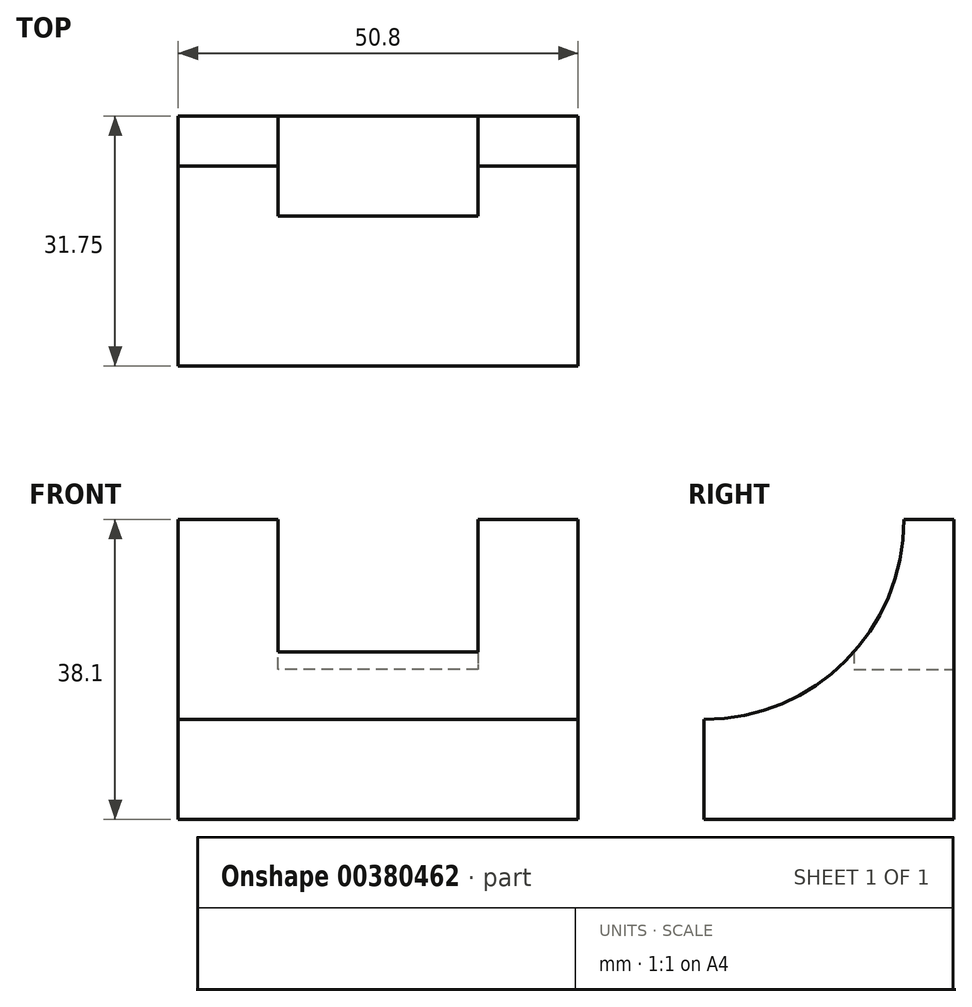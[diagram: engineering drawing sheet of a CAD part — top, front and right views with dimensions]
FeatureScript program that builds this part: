
annotation { "Feature Type Name" : "Feature", "Feature Type Description" : "" }
export const myFeature = defineFeature(function(context is Context, id is Id, definition is map)
    precondition{}
    {
        {
            var Q0;
            Q0=qCreatedBy(makeId("Front.planeOp"),FACE);
            var sketch = newSketch(context, id + "F0", { "sketchPlane" : qUnion([Q0])});
            skLineSegment(sketch, "E0", {"start": v(0, 38.1) * mm, "end": v(0, 0) * mm});
            skLineSegment(sketch, "E1", {"start": v(0, 0) * mm, "end": v(50.8, 0) * mm});
            skLineSegment(sketch, "E2", {"start": v(0, 38.1) * mm, "end": v(50.8, 38.1) * mm});
            skLineSegment(sketch, "E3", {"start": v(50.8, 38.1) * mm, "end": v(50.8, 0) * mm});
            skSolve(sketch);
        }
        {
            var Q0;
            Q0 = qSketchRegion(id + "F0", true);
            extrude(context, id + "F1", {"entities" : qUnion([Q0]), "depth" : 31.75 * mm});
        }
        {
            var Q0;
            Q0=makeQuery(id+"F1.opExtrude","CAP_FACE",FACE,{"disambiguationData":[OSD([sQuery(id+"F0.wireOp",EDGE,"E0"),sQuery(id+"F0.wireOp",EDGE,"E1"),sQuery(id+"F0.wireOp",EDGE,"E2"),sQuery(id+"F0.wireOp",EDGE,"E3")])],"isStart":true});
            var sketch = newSketch(context, id + "F2", { "sketchPlane" : qUnion([Q0])});
            skLineSegment(sketch, "E4", {"start": v(-38.1, 38.1) * mm, "end": v(-38.1, 19.05) * mm});
            skLineSegment(sketch, "E5", {"start": v(-38.1, 19.05) * mm, "end": v(-12.7, 19.05) * mm});
            skLineSegment(sketch, "E6", {"start": v(-12.7, 19.05) * mm, "end": v(-12.7, 38.1) * mm});
            skSolve(sketch);
        }
        {
            var Q0;
            Q0 = qSketchRegion(id + "F2", true);
            var Q1;
            {var subQ0=sQuery(id+"F2.wireOp",EDGE,"E4");Q1=makeQuery(id+"F2.imprint","IMPRINT",FACE,{"disambiguationData":[TD([[makeQuery(id+"F2.imprint","IMPRINT",EDGE,{"derivedFrom":subQ0}),1.0]])]});}
            extrude(context, id + "F3", {"entities" : qUnion([Q0, Q1]), "operationType" : NewBodyOperationType.REMOVE, "oppositeDirection" : true, "depth" : 12.7 * mm});
        }
        {
            var Q0;
            Q0=makeQuery(id+"F1.opExtrude","SWEPT_FACE",FACE,{"disambiguationData":[OSD([sQuery(id+"F0.wireOp",EDGE,"E3")])]});
            var sketch = newSketch(context, id + "F4", { "sketchPlane" : qUnion([Q0])});
            skCircle(sketch, "E7", {"center": v(-31.75, 38.1) * mm, "radius": 25.4 * mm});
            skSolve(sketch);
        }
        {
            var Q0;
            {var subQ0=sQuery(id+"F4.wireOp",EDGE,"E7");var subQ1=sQuery(id+"F0.wireOp",EDGE,"E3");var subQ4=makeQuery(id+"F1.opExtrude","CAP_EDGE",EDGE,{"disambiguationData":[OSD([subQ1])],"isStart":false});var subQ5=makeQuery(id+"F4.imprint","INTERSECT",VERTEX,{"derivedFrom":[subQ4,subQ0]});Q0=makeQuery(id+"F4.imprint","IMPRINT",FACE,{"disambiguationData":[TD([[makeQuery(id+"F4.imprint","IMPRINT",EDGE,{"disambiguationData":[TD([[subQ5,-1.0]])],"derivedFrom":subQ0}),1.0]])]});}
            var Q1;
            {var subQ0=sQuery(id+"F4.wireOp",EDGE,"E7");var subQ1=sQuery(id+"F0.wireOp",EDGE,"E3");var subQ4=makeQuery(id+"F1.opExtrude","CAP_EDGE",EDGE,{"disambiguationData":[OSD([subQ1])],"isStart":false});var subQ5=makeQuery(id+"F4.imprint","INTERSECT",VERTEX,{"derivedFrom":[subQ4,subQ0]});Q1=makeQuery(id+"F4.imprint","IMPRINT",FACE,{"disambiguationData":[TD([[makeQuery(id+"F4.imprint","IMPRINT",EDGE,{"disambiguationData":[TD([[subQ5,1.0]])],"derivedFrom":subQ0}),1.0]])]});}
            extrude(context, id + "F5", {"entities" : qUnion([Q0, Q1]), "operationType" : NewBodyOperationType.REMOVE, "oppositeDirection" : true, "depth" : 50.8 * mm});
        }
    });
